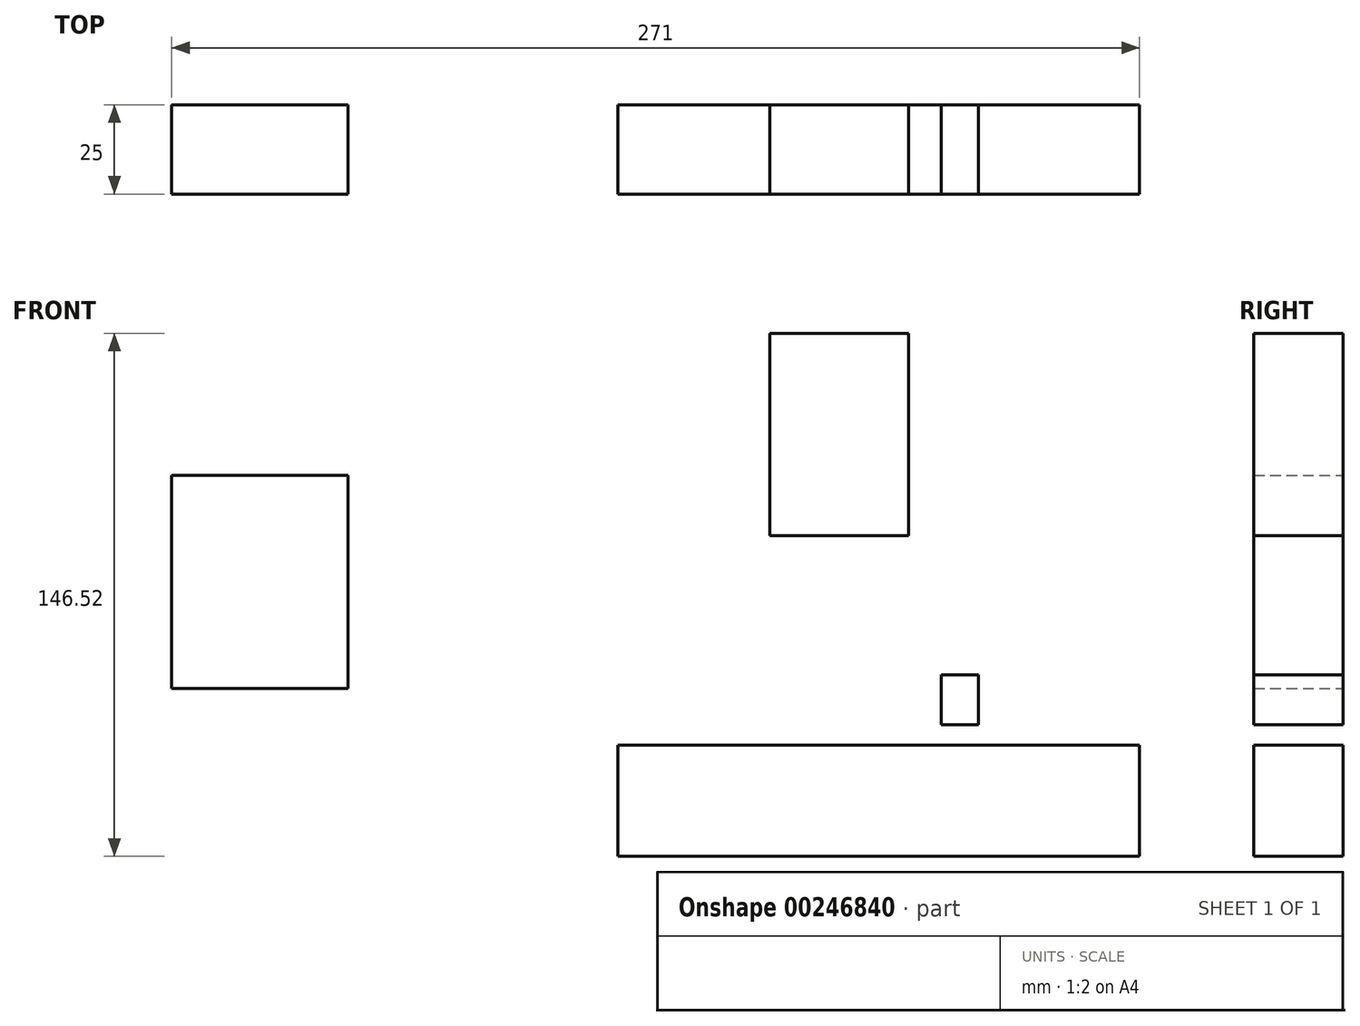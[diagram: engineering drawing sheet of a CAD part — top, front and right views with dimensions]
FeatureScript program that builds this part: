
annotation { "Feature Type Name" : "Feature", "Feature Type Description" : "" }
export const myFeature = defineFeature(function(context is Context, id is Id, definition is map)
    precondition{}
    {
        {
            var Q0;
            Q0=qCreatedBy(makeId("Front.planeOp"),FACE);
            var sketch = newSketch(context, id + "F0", { "sketchPlane" : qUnion([Q0])});
            skLineSegment(sketch, "E0.bottom", {"start": v(-116.2, 7.35) * mm, "end": v(-66.86, 7.35) * mm});
            skLineSegment(sketch, "E0.top", {"start": v(-116.2, 67.03) * mm, "end": v(-66.86, 67.03) * mm});
            skLineSegment(sketch, "E0.left", {"start": v(-116.2, 7.35) * mm, "end": v(-116.2, 67.03) * mm});
            skLineSegment(sketch, "E0.right", {"start": v(-66.86, 7.35) * mm, "end": v(-66.86, 67.03) * mm});
            skPoint(sketch, "E0.middle", {"position": v(-91.53, 37.2) * mm});
            skLineSegment(sketch, "E1.bottom", {"start": v(51.28, 50.18) * mm, "end": v(90.23, 50.18) * mm});
            skLineSegment(sketch, "E1.top", {"start": v(51.28, 106.86) * mm, "end": v(90.23, 106.86) * mm});
            skLineSegment(sketch, "E1.left", {"start": v(51.28, 50.18) * mm, "end": v(51.28, 106.86) * mm});
            skLineSegment(sketch, "E1.right", {"start": v(90.23, 50.18) * mm, "end": v(90.23, 106.86) * mm});
            skPoint(sketch, "E1.middle", {"position": v(70.75, 78.52) * mm});
            skLineSegment(sketch, "E2.bottom", {"start": v(99.31, -2.81) * mm, "end": v(109.7, -2.81) * mm});
            skLineSegment(sketch, "E2.top", {"start": v(99.31, 11.22) * mm, "end": v(109.7, 11.22) * mm});
            skLineSegment(sketch, "E2.left", {"start": v(99.31, -2.81) * mm, "end": v(99.31, 11.22) * mm});
            skLineSegment(sketch, "E2.right", {"start": v(109.7, -2.81) * mm, "end": v(109.7, 11.22) * mm});
            skPoint(sketch, "E2.middle", {"position": v(104.5, 4.2) * mm});
            skLineSegment(sketch, "E3.bottom", {"start": v(154.81, -8.54) * mm, "end": v(8.76, -8.54) * mm});
            skLineSegment(sketch, "E3.top", {"start": v(154.81, -39.66) * mm, "end": v(8.76, -39.66) * mm});
            skLineSegment(sketch, "E3.left", {"start": v(154.81, -8.54) * mm, "end": v(154.81, -39.66) * mm});
            skLineSegment(sketch, "E3.right", {"start": v(8.76, -8.54) * mm, "end": v(8.76, -39.66) * mm});
            skPoint(sketch, "E3.middle", {"position": v(81.79, -24.1) * mm});
            skSolve(sketch);
        }
        {
            var Q0;
            Q0=qSketchRegion(id+"F0",true);
            extrude(context, id + "F1", {"entities" : qUnion([Q0]), "depth" : 25 * mm});
        }
    });
